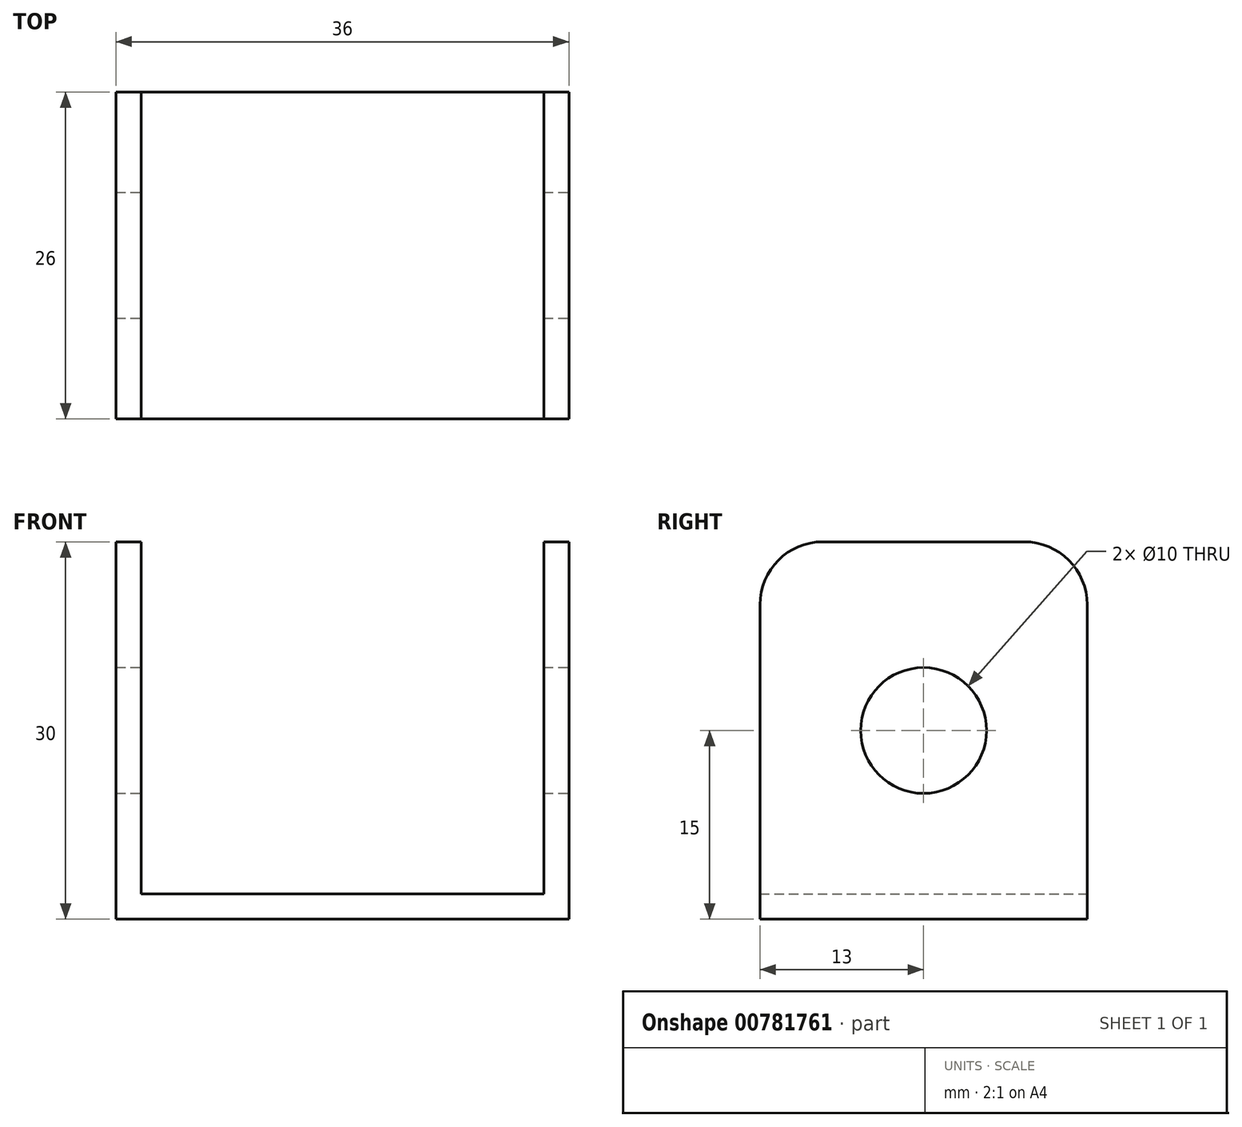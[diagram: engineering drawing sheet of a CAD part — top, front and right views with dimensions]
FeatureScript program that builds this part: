
annotation { "Feature Type Name" : "Feature", "Feature Type Description" : "" }
export const myFeature = defineFeature(function(context is Context, id is Id, definition is map)
    precondition{}
    {
        {
            var Q0;
            Q0=qCreatedBy(makeId("Front.planeOp"),FACE);
            var sketch = newSketch(context, id + "F0", { "sketchPlane" : qUnion([Q0])});
            skLineSegment(sketch, "E0.bottom", {"start": v(18, -15) * mm, "end": v(-18, -15) * mm});
            skLineSegment(sketch, "E0.top", {"start": v(18, 15) * mm, "end": v(16, 15) * mm});
            skLineSegment(sketch, "E0.left", {"start": v(18, -15) * mm, "end": v(18, 15) * mm});
            skLineSegment(sketch, "E0.right", {"start": v(-18, -15) * mm, "end": v(-18, 15) * mm});
            skPoint(sketch, "E0.middle", {"position": v(0, 0) * mm});
            skLineSegment(sketch, "E1", {"start": v(-16, 15) * mm, "end": v(-16, -13) * mm});
            skLineSegment(sketch, "E2", {"start": v(16, 15) * mm, "end": v(16, -13) * mm});
            skLineSegment(sketch, "E3", {"start": v(16, -13) * mm, "end": v(-16, -13) * mm});
            skLineSegment(sketch, "E4.trimOffspring", {"start": v(-16, 15) * mm, "end": v(-18, 15) * mm});
            skPoint(sketch, "E5.orphan", {"position": v(-18, -13) * mm});
            skSolve(sketch);
        }
        {
            var Q0;
            Q0=makeQuery(id+"F0.imprint","IMPRINT",FACE,{"disambiguationData":[TD([[makeQuery(id+"F0.imprint","IMPRINT",EDGE,{"derivedFrom":sQuery(id+"F0.wireOp",EDGE,"E0.bottom")}),-1.0]])]});
            extrude(context, id + "F1", {"entities" : qUnion([Q0]), "depth" : 26 * mm, "offsetDistance" : 25 * mm});
        }
        {
            var Q0;
            Q0=makeQuery(id+"F1.opExtrude","SWEPT_FACE",FACE,{"disambiguationData":[OSD([sQuery(id+"F0.wireOp",EDGE,"E0.left")])]});
            var sketch = newSketch(context, id + "F2", { "sketchPlane" : qUnion([Q0])});
            skCircle(sketch, "E6", {"center": v(-13, 0) * mm, "radius": 5 * mm});
            skPoint(sketch, "E6.centerSnap0", {"position": v(-13, 15) * mm});
            skSolve(sketch);
        }
        {
            var Q0;
            Q0=makeQuery(id+"F2.imprint","IMPRINT",FACE,{"disambiguationData":[TD([[makeQuery(id+"F2.imprint","IMPRINT",EDGE,{"derivedFrom":sQuery(id+"F2.wireOp",EDGE,"E6")}),1.0]])]});
            extrude(context, id + "F3", {"entities" : qUnion([Q0]), "operationType" : NewBodyOperationType.REMOVE, "oppositeDirection" : true, "depth" : 40 * mm, "offsetDistance" : 25 * mm});
        }
        {
            var Q0;
            Q0=makeQuery(id+"F1.opExtrude","CAP_EDGE",EDGE,{"disambiguationData":[OSD([sQuery(id+"F0.wireOp",EDGE,"E4.trimOffspring")])],"isStart":true});
            var Q1;
            Q1=makeQuery(id+"F1.opExtrude","CAP_EDGE",EDGE,{"disambiguationData":[OSD([sQuery(id+"F0.wireOp",EDGE,"E0.top")])],"isStart":true});
            var Q2;
            Q2=makeQuery(id+"F1.opExtrude","CAP_EDGE",EDGE,{"disambiguationData":[OSD([sQuery(id+"F0.wireOp",EDGE,"E4.trimOffspring")])],"isStart":false});
            var Q3;
            Q3=makeQuery(id+"F1.opExtrude","CAP_EDGE",EDGE,{"disambiguationData":[OSD([sQuery(id+"F0.wireOp",EDGE,"E0.top")])],"isStart":false});
            fillet(context, id + "F4", {"entities" : qUnion([Q0, Q1, Q2, Q3]), "radius" : 5 * mm, "tangentPropagation" : true, "allowEdgeOverflow" : false});
        }
    });
